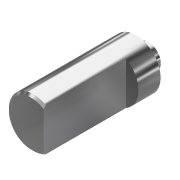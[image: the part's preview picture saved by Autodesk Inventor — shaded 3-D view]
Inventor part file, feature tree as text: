
AUTODESK INVENTOR PART (.ipt)
format: ipt  version: 2014 (Build 180170000, 170)  size: 97,792 bytes
history: native  units: in
note: dims shown in document units (in); Inventor stores cm internally (conversion verified against a paired STEP export)
features: extrude x3, sketch x3, chamfer x1
ambient origin geometry x8: Origin, YZ Plane, XZ Plane, XY Plane, X Axis, Y Axis, Z Axis, Center Point
bodies: Solid1 (feature_tree)
feature tree (7):
  extrude  "Extrusion1"  Depth=0.5in TaperAngle=0.0deg
  extrude  "Extrusion2"  Depth=0.0585in TaperAngle=0.0deg
  extrude  "Extrusion3"  Depth=0.06in TaperAngle=45.0deg
  chamfer  "Chamfer1"  [1 undecoded]
  sketch  "Sketch1"  dims[d0=0.235in d1=0.5in d2=0.0in]
  sketch  "Sketch2"  dims[d3=0.0585in d4=0.394in d5=0.0in]
  sketch  "Sketch3"  dims[d6=0.06in d7=0.0in d8=0.01in d9=0.125in d10=45.0deg]
note: 1 required parameter value undecoded (feature->parameter linkage not recoverable at this tier; creation-order binding heuristic only, values carry confidence <= 0.55)
